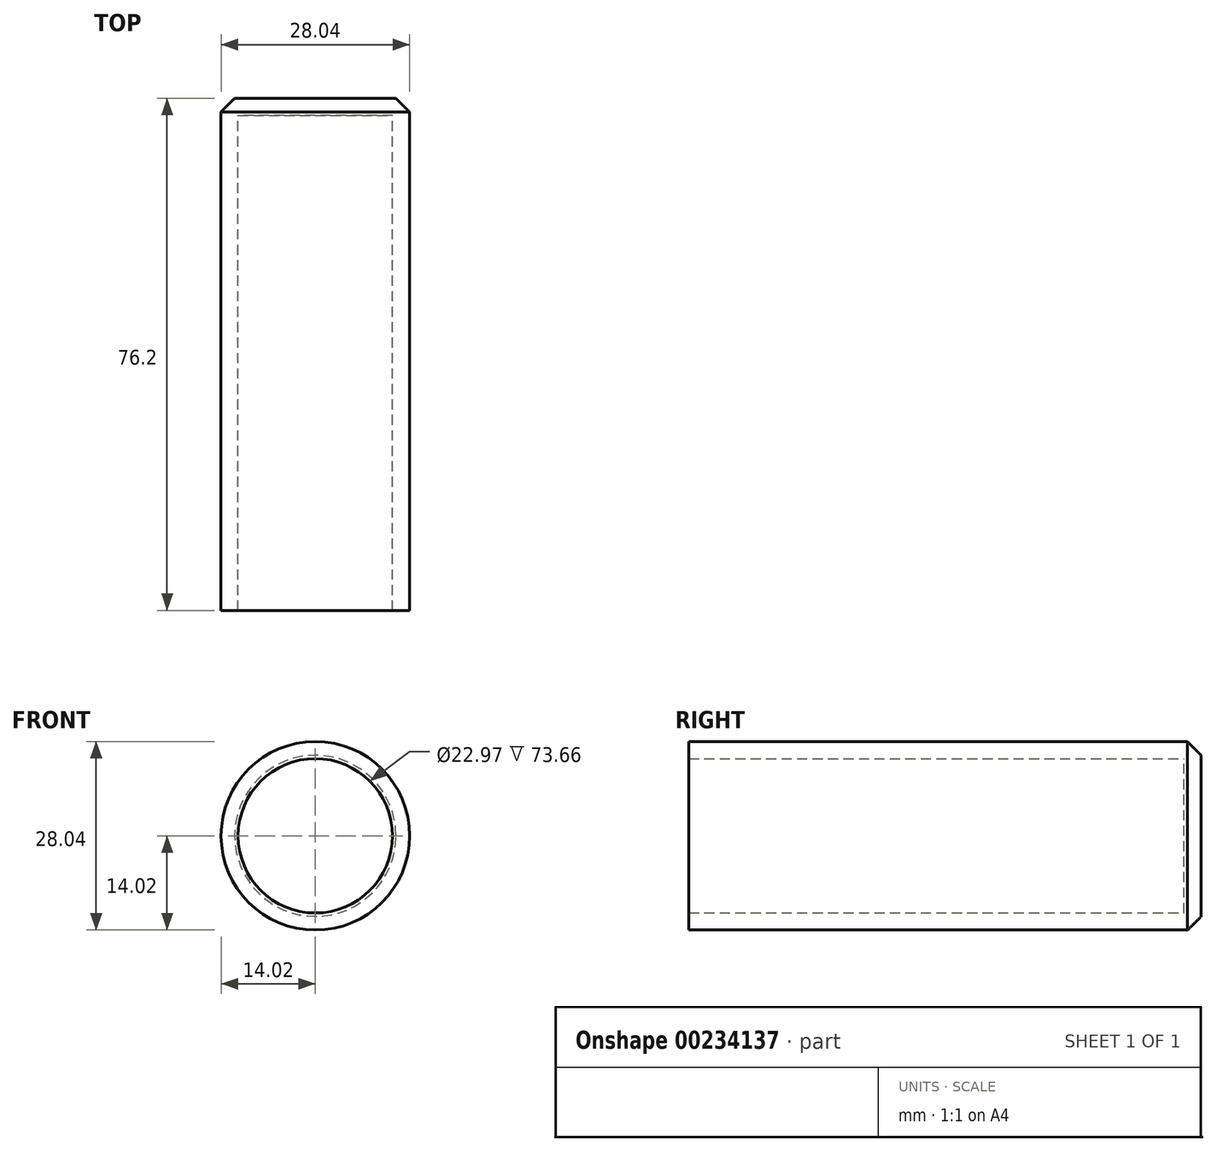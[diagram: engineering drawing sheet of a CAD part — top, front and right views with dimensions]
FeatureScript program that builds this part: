
annotation { "Feature Type Name" : "Feature", "Feature Type Description" : "" }
export const myFeature = defineFeature(function(context is Context, id is Id, definition is map)
    precondition{}
    {
        {
            var Q0;
            Q0=qCreatedBy(makeId("Front.planeOp"),FACE);
            var sketch = newSketch(context, id + "F2", { "sketchPlane" : qUnion([Q0])});
            skCircle(sketch, "E0", {"center": v(0, 0) * mm, "radius": 14.02 * mm});
            skSolve(sketch);
        }
        {
            var Q0;
            Q0=makeQuery(id+"F2.imprint","IMPRINT",FACE,{"disambiguationData":[TD([[makeQuery(id+"F2.imprint","IMPRINT",EDGE,{"derivedFrom":sQuery(id+"F2.wireOp",EDGE,"E0")}),1.0]])]});
            extrude(context, id + "F0", {"entities" : qUnion([Q0]), "depth" : 76.2 * mm});
        }
        {
            var Q0;
            Q0=makeQuery(id+"F0.opExtrude","CAP_FACE",FACE,{"disambiguationData":[OSD([sQuery(id+"F2.wireOp",EDGE,"E0")])],"isStart":false});
            shell(context, id + "F1", {"entities" : qUnion([Q0]), "thickness" : 2.54 * mm});
        }
        {
            var Q0;
            Q0=makeQuery(id+"F0.opExtrude","CAP_EDGE",EDGE,{"disambiguationData":[OSD([sQuery(id+"F2.wireOp",EDGE,"E0")])],"isStart":true});
            chamfer(context, id + "F3", {"entities" : qUnion([Q0]), "width" : 2.03 * mm, "tangentPropagation" : true});
        }
    });
